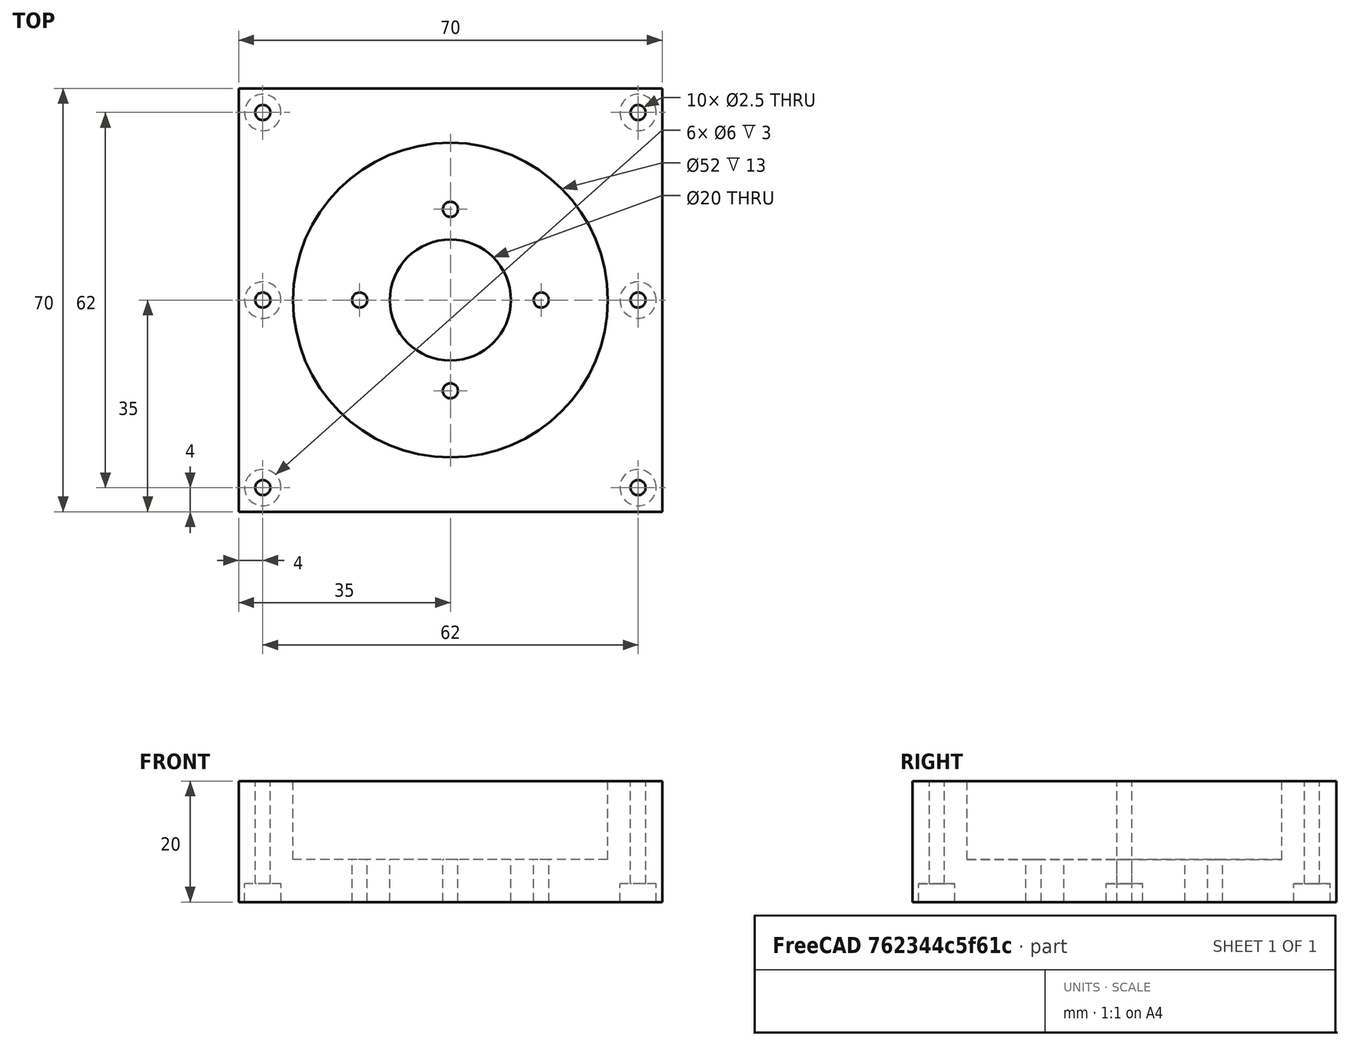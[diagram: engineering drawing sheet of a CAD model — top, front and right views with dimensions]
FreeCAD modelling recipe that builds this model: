
FCSTD DOCUMENT  (FreeCAD 0.17RUnknown)
Label: lager
License: All rights reserved
LicenseURL: http://en.wikipedia.org/wiki/All_rights_reserved
objects: Part::Cylinder×18, Part::Cut×4, Part::MultiFuse×4, Part::Box×1
note: 27 computed .brp shape members not serialized (recipe doc carries the construction recipe); baked Part::Feature solids carry a one-line shape summary decoded from their .brp

FEATURE [Part::Box] Box  label="Würfel"
  AttacherType = Attacher::AttachEngine3D
  Height = 20
  Length = 70
  Placement = pos=(-35,-35,0) rot=(0,0,1;0rad)
  Width = 70
FEATURE [Part::Cylinder] Cylinder  label="Zylinder"
  Angle = 360
  AttacherType = Attacher::AttachEngine3D
  Height = 20
  Radius = 10
FEATURE [Part::Cut] Cut
  Base = -> Box
  Tool = -> Cylinder
FEATURE [Part::Cylinder] Cylinder001  label="Zylinder001"
  Angle = 360
  AttacherType = Attacher::AttachEngine3D
  Height = 13
  Placement = pos=(0,0,7) rot=(0,0,1;0rad)
  Radius = 26
FEATURE [Part::Cut] Cut001
  Base = -> Cut
  Tool = -> Cylinder001
FEATURE [Part::Cylinder] Cylinder002  label="Zylinder002"
  Angle = 360
  AttacherType = Attacher::AttachEngine3D
  Height = 7
  Placement = pos=(15,0,0) rot=(0,0,1;0rad)
  Radius = 1.25
FEATURE [Part::Cylinder] Cylinder003  label="Zylinder003"
  Angle = 360
  AttacherType = Attacher::AttachEngine3D
  Height = 7
  Placement = pos=(-15,0,0) rot=(0,0,1;0rad)
  Radius = 1.25
FEATURE [Part::Cylinder] Cylinder004  label="Zylinder004"
  Angle = 360
  AttacherType = Attacher::AttachEngine3D
  Height = 7
  Placement = pos=(0,15,0) rot=(0,0,1;0rad)
  Radius = 1.25
FEATURE [Part::Cylinder] Cylinder005  label="Zylinder005"
  Angle = 360
  AttacherType = Attacher::AttachEngine3D
  Height = 7
  Placement = pos=(0,-15,0) rot=(0,0,1;0rad)
  Radius = 1.25
FEATURE [Part::MultiFuse] Fusion
  Shapes = -> [Cylinder002,Cylinder003,Cylinder005,Cylinder004]
FEATURE [Part::Cut] Cut002
  Base = -> Cut001
  Tool = -> Fusion
FEATURE [Part::Cylinder] Cylinder006  label="Zylinder006"
  Angle = 360
  AttacherType = Attacher::AttachEngine3D
  Height = 20
  Placement = pos=(31,31,0) rot=(0,0,1;0rad)
  Radius = 1.25
FEATURE [Part::Cylinder] Cylinder007  label="Zylinder007"
  Angle = 360
  AttacherType = Attacher::AttachEngine3D
  Height = 20
  Placement = pos=(31,0,0) rot=(0,0,1;0rad)
  Radius = 1.25
FEATURE [Part::Cylinder] Cylinder008  label="Zylinder008"
  Angle = 360
  AttacherType = Attacher::AttachEngine3D
  Height = 20
  Placement = pos=(31,-31,0) rot=(0,0,1;0rad)
  Radius = 1.25
FEATURE [Part::Cylinder] Cylinder009  label="Zylinder009"
  Angle = 360
  AttacherType = Attacher::AttachEngine3D
  Height = 20
  Placement = pos=(-31,31,0) rot=(0,0,1;0rad)
  Radius = 1.25
FEATURE [Part::Cylinder] Cylinder010  label="Zylinder010"
  Angle = 360
  AttacherType = Attacher::AttachEngine3D
  Height = 20
  Placement = pos=(-31,-31,0) rot=(0,0,1;0rad)
  Radius = 1.25
FEATURE [Part::Cylinder] Cylinder011  label="Zylinder011"
  Angle = 360
  AttacherType = Attacher::AttachEngine3D
  Height = 20
  Placement = pos=(-31,0,0) rot=(0,0,1;0rad)
  Radius = 1.25
FEATURE [Part::Cylinder] Cylinder012  label="Zylinder012"
  Angle = 360
  AttacherType = Attacher::AttachEngine3D
  Height = 3
  Placement = pos=(31,31,0) rot=(0,0,1;0rad)
  Radius = 3
FEATURE [Part::Cylinder] Cylinder013  label="Zylinder013"
  Angle = 360
  AttacherType = Attacher::AttachEngine3D
  Height = 3
  Placement = pos=(-31,31,0) rot=(0,0,1;0rad)
  Radius = 3
FEATURE [Part::Cylinder] Cylinder014  label="Zylinder014"
  Angle = 360
  AttacherType = Attacher::AttachEngine3D
  Height = 3
  Placement = pos=(-31,-31,0) rot=(0,0,1;0rad)
  Radius = 3
FEATURE [Part::Cylinder] Cylinder015  label="Zylinder015"
  Angle = 360
  AttacherType = Attacher::AttachEngine3D
  Height = 3
  Placement = pos=(31,-31,0) rot=(0,0,1;0rad)
  Radius = 3
FEATURE [Part::Cylinder] Cylinder016  label="Zylinder016"
  Angle = 360
  AttacherType = Attacher::AttachEngine3D
  Height = 3
  Placement = pos=(31,0,0) rot=(0,0,1;0rad)
  Radius = 3
FEATURE [Part::Cylinder] Cylinder017  label="Zylinder017"
  Angle = 360
  AttacherType = Attacher::AttachEngine3D
  Height = 3
  Placement = pos=(-31,0,0) rot=(0,0,1;0rad)
  Radius = 3
FEATURE [Part::MultiFuse] Fusion001
  Shapes = -> [Cylinder012,Cylinder013,Cylinder017,Cylinder014,Cylinder015,Cylinder016]
FEATURE [Part::MultiFuse] Fusion002
  Shapes = -> [Cylinder006,Cylinder009,Cylinder010,Cylinder008,Cylinder011,Cylinder007]
FEATURE [Part::MultiFuse] Fusion003
  Shapes = -> [Fusion001,Fusion002]
FEATURE [Part::Cut] Cut003
  Base = -> Cut002
  Tool = -> Fusion003
